FCSTD DOCUMENT  (FreeCAD 0.18R15419 (Git))
Label: RESISTENCIA
License: All rights reserved
LicenseURL: http://en.wikipedia.org/wiki/All_rights_reserved
objects: Part::Helix×2, Part::FeaturePython×2, Part::Circle×1, Part::Sweep×1, Part::Cylinder×1, Part::Torus×1, Part::MultiFuse×1, Part::Compound×1
note: 10 computed .brp shape members not serialized (recipe doc carries the construction recipe); baked Part::Feature solids carry a one-line shape summary decoded from their .brp

FEATURE [Part::Circle] Circle
  Angle0 = 0
  Angle1 = 360
  AttacherType = Attacher::AttachEngine3D
  Placement = pos=(1,0,0) rot=(1,0,0;1.5708rad)
  Radius = 0.25
FEATURE [Part::Helix] Helix
  Angle = 0
  AttacherType = Attacher::AttachEngine3D
  Height = 1
  LocalCoord = 0
  Pitch = 1
  Radius = 1
  Style = 1
FEATURE [Part::Helix] Helix001
  Angle = 0
  AttacherType = Attacher::AttachEngine3D
  Height = 30
  LocalCoord = 0
  Pitch = 10
  Radius = 29
  Style = 1
FEATURE [Part::Sweep] Sweep
  Frenet = true
  Placement = pos=(29,0,0) rot=(0.707107,0,0.707107;3.14159rad)
  Sections = -> [Circle]
  Solid = true
  Spine = -> Helix [Edge1]
  Transition = 1
FEATURE [Part::FeaturePython] PathArray  # WARN: FeaturePython — macro-defined, semantics opaque (R4)
  Align = true
  Base = -> Sweep
  Count = 570
  PathObj = -> Helix001
  Xlate = (0,0,0)
FEATURE [Part::Cylinder] Cylinder
  Angle = 360
  AttacherType = Attacher::AttachEngine3D
  Height = 10
  Placement = pos=(1,0,0) rot=(1,0,0;1.5708rad)
  Radius = 0.25
FEATURE [Part::Torus] Torus
  Angle1 = -180
  Angle2 = 180
  Angle3 = 90
  AttacherType = Attacher::AttachEngine3D
  Radius1 = 1
  Radius2 = 0.25
FEATURE [Part::MultiFuse] Fusion
  Placement = pos=(31,-4e-16,4e-16) rot=(-0.57735,0.57735,-0.57735;4.18879rad)
  Shapes = -> [Cylinder,Torus]
FEATURE [Part::FeaturePython] Clone  label="Fusion001"  # Draft clone (typed FeaturePython)
  AttacherType = Attacher::AttachEngine3D
  Fuse = false
  Objects = -> [Fusion]
  Placement = pos=(31,1,30.05) rot=(0.57735,-0.57735,-0.57735;4.18879rad)
  Scale = (1,1,1)
FEATURE [Part::Compound] Compound
  Links = -> [Fusion,Clone,PathArray]
  Placement = pos=(0,0,0) rot=(1,0,0;1.5708rad)
